# Revit family: Faucet-Wall_Mount-Bath-KOHLER-July-K-16094IN_1
name_source: partatom
category: Plumbing Fixtures
revit_build: Autodesk Revit 2017 (Build: 20160225_1515(x64)
units: mm (PartAtom-declared; Revit-internal decimal feet)

## family parameters
Cut with Voids When Loaded = No
Host = Face
OmniClass Number = 23.31.11.00
OmniClass Title = Faucets
Part Type = Normal
Room Calculation Point = No
Round Connector Dimension = Use Diameter
Shared = No

## types (5) — shared parameters
ADA Compliant = No
Assembly Code = D2010
CW Connection = Yes
Cold Water Inlet = Cold Water Inlet
Date Modified = 12/29/2020
Default Elevation = 36"
Description = 2 WAY BIB TAP
Drain Included = No
Flow Rate = 0 GPM
HW Connection = No
Handle Clearance = 2 11/16"
Height = 2 3/8"
Hot Water Inlet = Hot Water Inlet
Length = 4 15/16"
Manufacturer = KOHLER Co.
Master Format 2014 = 22 41 39
Master Format 2014 Name = Residential Faucets, Supplies, and Trim
Material = Premium Metal Construction
Pressure = 0.00 psi
Product Documentation Link = http://resources.kohler.com
Product Name = July
Product Page URL = https://www.kohler.co.in
Spout Reach = 4 15/16"
URL = https://www.kohler.co.in
Vent Connection = No
Waste Connection = No
Waste Water Outlet = Waste Water Outlet
WaterSense Certified = No
Width = 2 3/8"

## per-type parameters (varying)
| type | Finish | Model | Type |
| CP-Polished Chrome | Kohler-Metal-CP-Polished_Chrome | K-16094IN-4-CP | 1 |
| AF-Flange Gold | Kohler-Metal-AF-Vibrant_French_Gold | K-16094IN-4-AF | 2 |
| BN-Brushed Nickel | Kohler-Metal-BN-Vibrant_Brushed_Nickel | K-16094IN-4-BN | 3 |
| BV-Brushed Bronze | Kohler-Metal-BV-Brushed_Bronze | K-16094IN-4-BV | 4 |
| RGD-Rose Gold | Kohler-Metal-RGD-Polished_Rose_Gold | K-16094IN-4-RGD | 5 |

## geometry (parser evidence)
native form markers: Sweep x4
no freeform markers — native parametric forms only
